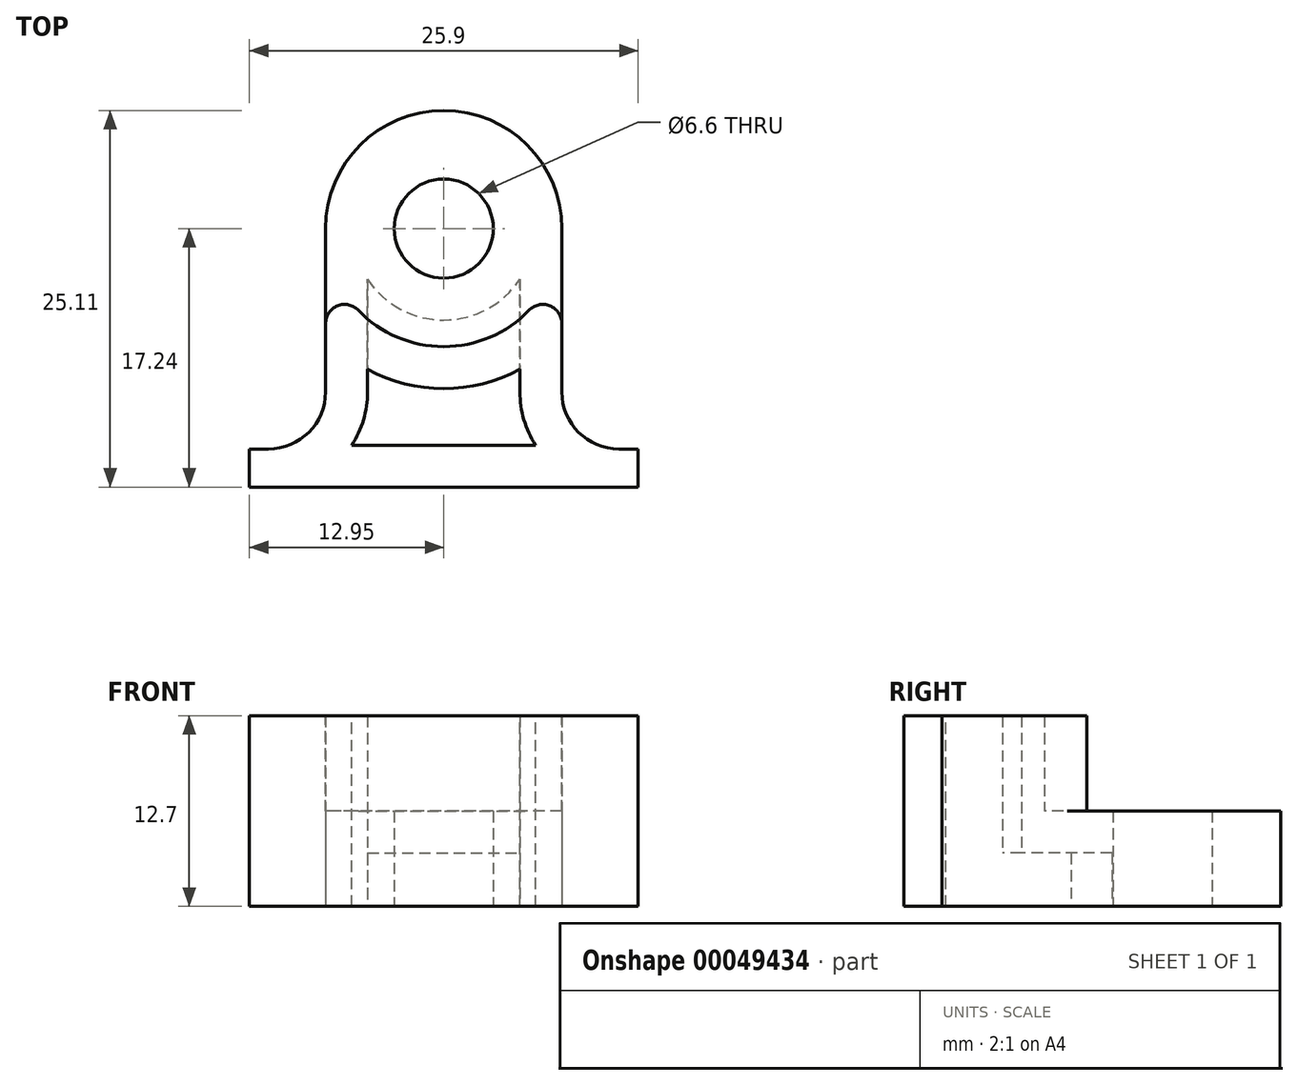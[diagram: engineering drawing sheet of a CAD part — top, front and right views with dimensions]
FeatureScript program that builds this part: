
annotation { "Feature Type Name" : "Feature", "Feature Type Description" : "" }
export const myFeature = defineFeature(function(context is Context, id is Id, definition is map)
    precondition{}
    {
        {
            var Q0;
            Q0=qCreatedBy(makeId("Top.planeOp"),FACE);
            var sketch = newSketch(context, id + "F0", { "sketchPlane" : qUnion([Q0])});
            skCircle(sketch, "E0", {"center": v(0, 0) * mm, "radius": 3.3 * mm});
            skSolve(sketch);
        }
        {
            var Q0;
            Q0=qCreatedBy(makeId("Top.planeOp"),FACE);
            var sketch = newSketch(context, id + "F1", { "sketchPlane" : qUnion([Q0])});
            skCircle(sketch, "E1", {"center": v(0, 0) * mm, "radius": 7.87 * mm});
            skSolve(sketch);
        }
        {
            var Q0;
            Q0=qCreatedBy(makeId("Top.planeOp"),FACE);
            var sketch = newSketch(context, id + "F2", { "sketchPlane" : qUnion([Q0])});
            skLineSegment(sketch, "E2", {"start": v(-7.87, 0) * mm, "end": v(-7.87, -14.7) * mm});
            skLineSegment(sketch, "E3", {"start": v(-7.87, -14.7) * mm, "end": v(7.87, -14.7) * mm});
            skLineSegment(sketch, "E4", {"start": v(7.87, -14.7) * mm, "end": v(7.87, 0) * mm});
            skArc(sketch, "E5", {"start": v(-7.87, 0) * mm, "mid": v(0, -7.87) * mm, "end": v(7.87, 0) * mm});
            skLineSegment(sketch, "E6", {"start": v(-7.87, -14.7) * mm, "end": v(-12.95, -14.7) * mm});
            skLineSegment(sketch, "E7", {"start": v(-12.95, -14.7) * mm, "end": v(-12.95, -17.24) * mm});
            skLineSegment(sketch, "E8", {"start": v(-12.95, -17.24) * mm, "end": v(12.95, -17.24) * mm});
            skLineSegment(sketch, "E9", {"start": v(12.95, -17.24) * mm, "end": v(12.95, -14.7) * mm});
            skLineSegment(sketch, "E10", {"start": v(12.95, -14.7) * mm, "end": v(7.87, -14.7) * mm});
            skSolve(sketch);
        }
        {
            var Q0;
            Q0=makeQuery(id+"F2.imprint","IMPRINT",FACE,{"disambiguationData":[TD([[makeQuery(id+"F2.imprint","IMPRINT",EDGE,{"derivedFrom":sQuery(id+"F2.wireOp",EDGE,"E3")}),-1.0]])]});
            var Q1;
            Q1=makeQuery(id+"F2.imprint","IMPRINT",FACE,{"disambiguationData":[TD([[makeQuery(id+"F2.imprint","IMPRINT",EDGE,{"derivedFrom":sQuery(id+"F2.wireOp",EDGE,"E2")}),1.0]])]});
            extrude(context, id + "F3", {"entities" : qUnion([Q0, Q1]), "depth" : 12.7 * mm});
        }
        {
            var Q0;
            Q0=qSketchRegion(id+"F1",true);
            extrude(context, id + "F4", {"entities" : qUnion([Q0]), "operationType" : NewBodyOperationType.ADD, "depth" : 6.35 * mm});
        }
        {
            var Q0;
            Q0=qSketchRegion(id+"F0",true);
            extrude(context, id + "F5", {"entities" : qUnion([Q0]), "operationType" : NewBodyOperationType.REMOVE, "depth" : 6.35 * mm});
        }
        {
            var Q0;
            Q0=makeQuery(id+"F3.opExtrude","SWEPT_EDGE",EDGE,{"disambiguationData":[OSD([sQuery(id+"F2.wireOp",EDGE,"E2"),sQuery(id+"F2.wireOp",EDGE,"E3"),sQuery(id+"F2.wireOp",EDGE,"E6")])]});
            var Q1;
            Q1=makeQuery(id+"F3.opExtrude","SWEPT_EDGE",EDGE,{"disambiguationData":[OSD([sQuery(id+"F2.wireOp",EDGE,"E3"),sQuery(id+"F2.wireOp",EDGE,"E4"),sQuery(id+"F2.wireOp",EDGE,"E10")])]});
            fillet(context, id + "F6", {"entities" : qUnion([Q0, Q1]), "radius" : 3.8 * mm, "tangentPropagation" : true, "allowEdgeOverflow" : false});
        }
        {
            var Q0;
            {var subQ0=sQuery(id+"F2.wireOp",EDGE,"E2");var subQ1=sQuery(id+"F2.wireOp",EDGE,"E5");Q0=makeQuery(id+"F4.boolean.opBoolean","SPLIT",EDGE,{"disambiguationData":[TD([makeQuery(id+"F3.opExtrude","CAP_FACE",FACE,{"disambiguationData":[OSD([subQ0,sQuery(id+"F2.wireOp",EDGE,"E4"),subQ1,sQuery(id+"F2.wireOp",EDGE,"E6"),sQuery(id+"F2.wireOp",EDGE,"E7"),sQuery(id+"F2.wireOp",EDGE,"E8"),sQuery(id+"F2.wireOp",EDGE,"E9"),sQuery(id+"F2.wireOp",EDGE,"E10")])],"isStart":false})])],"derivedFrom":makeQuery(id+"F3.opExtrude","SWEPT_EDGE",EDGE,{"disambiguationData":[OSD([subQ0,subQ1])]})});}
            var Q1;
            {var subQ0=sQuery(id+"F2.wireOp",EDGE,"E4");var subQ1=sQuery(id+"F2.wireOp",EDGE,"E5");Q1=makeQuery(id+"F4.boolean.opBoolean","SPLIT",EDGE,{"disambiguationData":[TD([makeQuery(id+"F3.opExtrude","CAP_FACE",FACE,{"disambiguationData":[OSD([sQuery(id+"F2.wireOp",EDGE,"E2"),subQ0,subQ1,sQuery(id+"F2.wireOp",EDGE,"E6"),sQuery(id+"F2.wireOp",EDGE,"E7"),sQuery(id+"F2.wireOp",EDGE,"E8"),sQuery(id+"F2.wireOp",EDGE,"E9"),sQuery(id+"F2.wireOp",EDGE,"E10")])],"isStart":false})])],"derivedFrom":makeQuery(id+"F3.opExtrude","SWEPT_EDGE",EDGE,{"disambiguationData":[OSD([subQ0,subQ1])]})});}
            fillet(context, id + "F7", {"entities" : qUnion([Q0, Q1]), "radius" : 1.27 * mm, "tangentPropagation" : true, "allowEdgeOverflow" : false});
        }
        {
            var Q0;
            Q0=makeQuery(id+"F3.opExtrude","CAP_FACE",FACE,{"disambiguationData":[OSD([sQuery(id+"F2.wireOp",EDGE,"E2"),sQuery(id+"F2.wireOp",EDGE,"E4"),sQuery(id+"F2.wireOp",EDGE,"E5"),sQuery(id+"F2.wireOp",EDGE,"E6"),sQuery(id+"F2.wireOp",EDGE,"E7"),sQuery(id+"F2.wireOp",EDGE,"E8"),sQuery(id+"F2.wireOp",EDGE,"E9"),sQuery(id+"F2.wireOp",EDGE,"E10")])],"isStart":false});
            shell(context, id + "F8", {"entities" : qUnion([Q0]), "thickness" : 2.8 * mm});
        }
        {
            var Q0;
            Q0=makeQuery(id+"F8.opShell","OFFSET_FACE",FACE,{"disambiguationData":[OSD([sQuery(id+"F1.wireOp",EDGE,"E1"),sQuery(id+"F2.wireOp",EDGE,"E2"),sQuery(id+"F2.wireOp",EDGE,"E4"),sQuery(id+"F2.wireOp",EDGE,"E5"),sQuery(id+"F2.wireOp",EDGE,"E6"),sQuery(id+"F2.wireOp",EDGE,"E7"),sQuery(id+"F2.wireOp",EDGE,"E8"),sQuery(id+"F2.wireOp",EDGE,"E9"),sQuery(id+"F2.wireOp",EDGE,"E10")])]});
            extrude(context, id + "F9", {"entities" : qUnion([Q0]), "operationType" : NewBodyOperationType.REMOVE, "oppositeDirection" : true, "depth" : 25.4 * mm});
        }
    });
